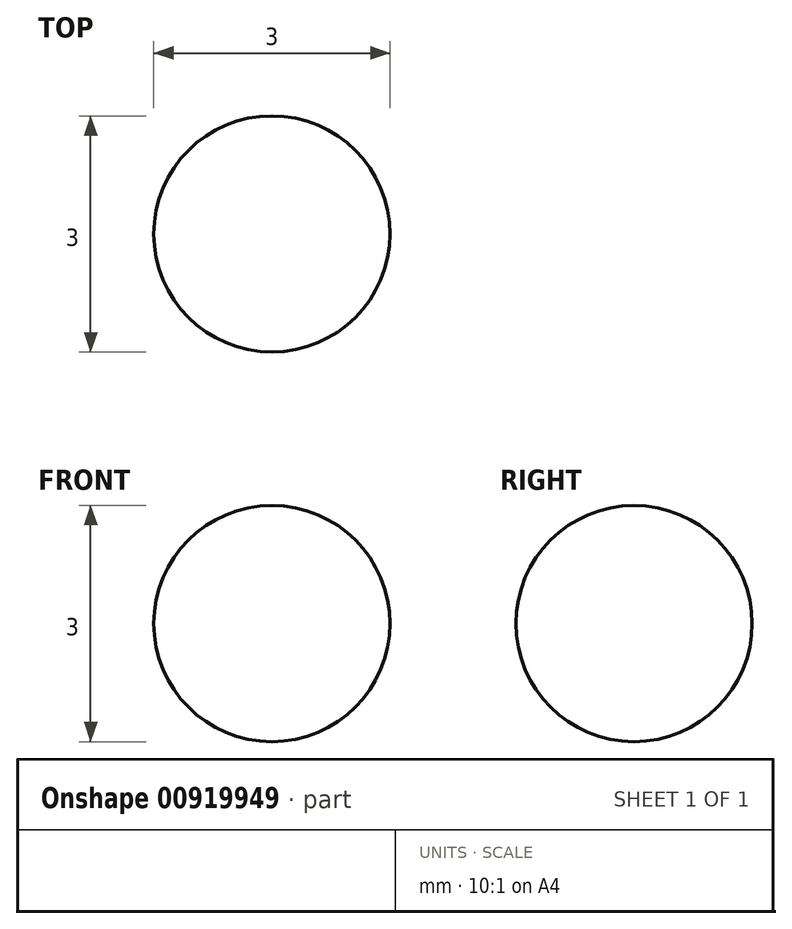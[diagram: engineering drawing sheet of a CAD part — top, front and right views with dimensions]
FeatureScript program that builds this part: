
annotation { "Feature Type Name" : "Feature", "Feature Type Description" : "" }
export const myFeature = defineFeature(function(context is Context, id is Id, definition is map)
    precondition{}
    {
        {
            var Q0;
            Q0=qCreatedBy(makeId("Front.planeOp"),FACE);
            var sketch = newSketch(context, id + "F0", { "sketchPlane" : qUnion([Q0])});
            skLineSegment(sketch, "E0", {"start": v(0, 3.44) * mm, "end": v(0, -3.44) * mm, "construction": true});
            skArc(sketch, "E1", {"start": v(0, 1.5) * mm, "mid": v(-1.5, 0) * mm, "end": v(0, -1.5) * mm});
            skLineSegment(sketch, "E2", {"start": v(0, 1.5) * mm, "end": v(0, -1.5) * mm});
            skSolve(sketch);
        }
        {
            var Q0;
            Q0=makeQuery(id+"F0.imprint","IMPRINT",FACE,{"disambiguationData":[TD([[makeQuery(id+"F0.imprint","IMPRINT",EDGE,{"derivedFrom":sQuery(id+"F0.wireOp",EDGE,"E1")}),1.0]])]});
            var Q1;
            Q1=sQuery(id+"F0.wireOp",EDGE,"E0");
            revolve(context, id + "F1", {"surfaceOperationType" : NewSurfaceOperationType.NEW, "entities" : qUnion([Q0]), "axis" : qUnion([Q1]), "revolveType" : RevolveType.FULL});
        }
    });
